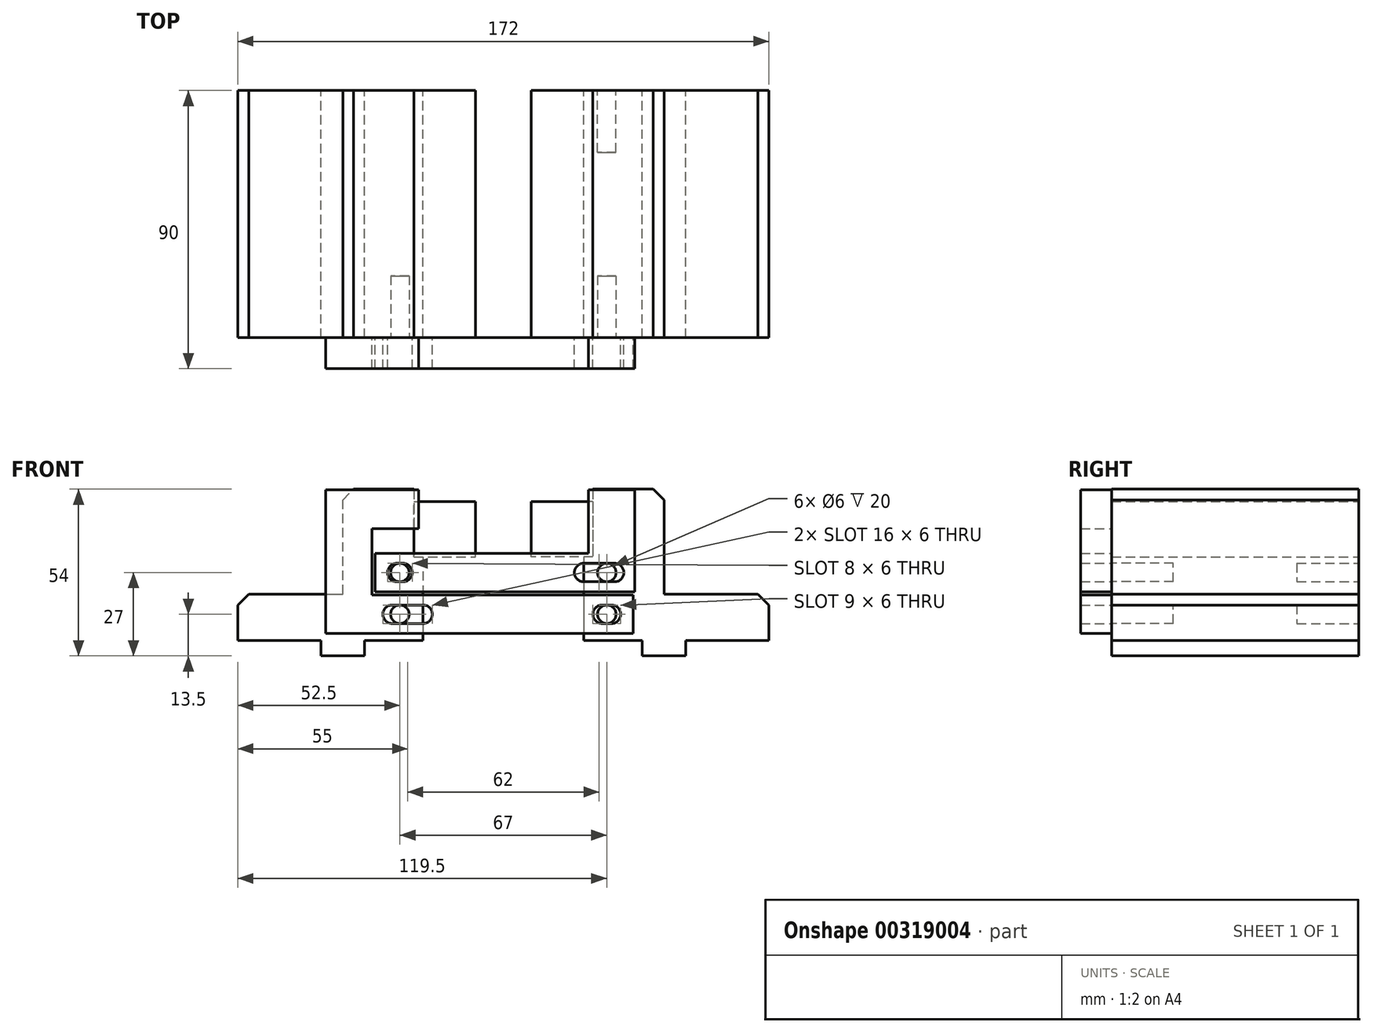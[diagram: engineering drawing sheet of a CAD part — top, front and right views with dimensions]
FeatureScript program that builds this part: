
annotation { "Feature Type Name" : "Feature", "Feature Type Description" : "" }
export const myFeature = defineFeature(function(context is Context, id is Id, definition is map)
    precondition{}
    {
        {
            var Q0;
            Q0=qCreatedBy(makeId("Front.planeOp"),FACE);
            var sketch = newSketch(context, id + "F0", { "sketchPlane" : qUnion([Q0])});
            skLineSegment(sketch, "E0", {"start": v(-26, 0) * mm, "end": v(-45, 0) * mm});
            skLineSegment(sketch, "E1", {"start": v(-45, 0) * mm, "end": v(-45, -5) * mm});
            skLineSegment(sketch, "E2", {"start": v(-45, -5) * mm, "end": v(-59, -5) * mm});
            skLineSegment(sketch, "E3", {"start": v(-59, -5) * mm, "end": v(-59, 0) * mm});
            skLineSegment(sketch, "E4", {"start": v(-59, 0) * mm, "end": v(-86, 0) * mm});
            skLineSegment(sketch, "E5", {"start": v(-86, 0) * mm, "end": v(-86, 11.46) * mm});
            skLineSegment(sketch, "E6", {"start": v(-86, 11.46) * mm, "end": v(-82.46, 15) * mm});
            skLineSegment(sketch, "E7", {"start": v(-82.46, 15) * mm, "end": v(-52, 15) * mm});
            skLineSegment(sketch, "E8", {"start": v(-52, 15) * mm, "end": v(-52, 45.46) * mm});
            skLineSegment(sketch, "E9", {"start": v(-52, 45.46) * mm, "end": v(-48.46, 49) * mm});
            skLineSegment(sketch, "E10", {"start": v(-48.46, 49) * mm, "end": v(-29, 49) * mm});
            skLineSegment(sketch, "E11", {"start": v(-29, 49) * mm, "end": v(-29, 45) * mm});
            skLineSegment(sketch, "E12", {"start": v(-29, 45) * mm, "end": v(-26, 45) * mm});
            skLineSegment(sketch, "E13", {"start": v(-26, 45) * mm, "end": v(-26, 0) * mm});
            skLineSegment(sketch, "E14.MirrorCS", {"start": v(45, 0) * mm, "end": v(45, -5) * mm});
            skLineSegment(sketch, "E15.MirrorCS", {"start": v(59, -5) * mm, "end": v(59, 0) * mm});
            skLineSegment(sketch, "E16.MirrorCS", {"start": v(29, 45) * mm, "end": v(26, 45) * mm});
            skLineSegment(sketch, "E17.MirrorCS", {"start": v(29, 49) * mm, "end": v(29, 45) * mm});
            skLineSegment(sketch, "E18.MirrorCS", {"start": v(86, 11.46) * mm, "end": v(82.46, 15) * mm});
            skLineSegment(sketch, "E19.MirrorCS", {"start": v(52, 45.46) * mm, "end": v(48.46, 49) * mm});
            skLineSegment(sketch, "E20.MirrorCS", {"start": v(26, 0) * mm, "end": v(45, 0) * mm});
            skLineSegment(sketch, "E21.MirrorCS", {"start": v(45, -5) * mm, "end": v(59, -5) * mm});
            skLineSegment(sketch, "E22.MirrorCS", {"start": v(26, 45) * mm, "end": v(26, 0) * mm});
            skLineSegment(sketch, "E23.MirrorCS", {"start": v(86, 0) * mm, "end": v(86, 11.46) * mm});
            skLineSegment(sketch, "E24.MirrorCS", {"start": v(48.46, 49) * mm, "end": v(29, 49) * mm});
            skLineSegment(sketch, "E25.MirrorCS", {"start": v(52, 15) * mm, "end": v(52, 45.46) * mm});
            skLineSegment(sketch, "E26.MirrorCS", {"start": v(82.46, 15) * mm, "end": v(52, 15) * mm});
            skLineSegment(sketch, "E27.MirrorCS", {"start": v(59, 0) * mm, "end": v(86, 0) * mm});
            skSolve(sketch);
        }
        {
            var Q0;
            Q0=makeQuery(id+"F0.imprint","IMPRINT",FACE,{"disambiguationData":[TD([[makeQuery(id+"F0.imprint","IMPRINT",EDGE,{"derivedFrom":sQuery(id+"F0.wireOp",EDGE,"E0")}),-1.0]])]});
            var Q1;
            Q1=makeQuery(id+"F0.imprint","IMPRINT",FACE,{"disambiguationData":[TD([[makeQuery(id+"F0.imprint","IMPRINT",EDGE,{"derivedFrom":sQuery(id+"F0.wireOp",EDGE,"E14.MirrorCS")}),1.0]])]});
            extrude(context, id + "F1", {"entities" : qUnion([Q0, Q1]), "endBound" : BoundingType.SYMMETRIC, "depth" : 80 * mm});
        }
        {
            var Q0;
            Q0=makeQuery(id+"F1.opExtrude","CAP_FACE",FACE,{"disambiguationData":[OSD([sQuery(id+"F0.wireOp",EDGE,"E14.MirrorCS"),sQuery(id+"F0.wireOp",EDGE,"E15.MirrorCS"),sQuery(id+"F0.wireOp",EDGE,"E16.MirrorCS"),sQuery(id+"F0.wireOp",EDGE,"E17.MirrorCS"),sQuery(id+"F0.wireOp",EDGE,"E18.MirrorCS"),sQuery(id+"F0.wireOp",EDGE,"E19.MirrorCS"),sQuery(id+"F0.wireOp",EDGE,"E20.MirrorCS"),sQuery(id+"F0.wireOp",EDGE,"E21.MirrorCS"),sQuery(id+"F0.wireOp",EDGE,"E22.MirrorCS"),sQuery(id+"F0.wireOp",EDGE,"E23.MirrorCS"),sQuery(id+"F0.wireOp",EDGE,"E24.MirrorCS"),sQuery(id+"F0.wireOp",EDGE,"E25.MirrorCS"),sQuery(id+"F0.wireOp",EDGE,"E26.MirrorCS"),sQuery(id+"F0.wireOp",EDGE,"E27.MirrorCS")])],"isStart":true});
            var sketch = newSketch(context, id + "F2", { "sketchPlane" : qUnion([Q0])});
            skLineSegment(sketch, "E28", {"start": v(-29, 45) * mm, "end": v(-29, 27) * mm});
            skLineSegment(sketch, "E29", {"start": v(-29, 27) * mm, "end": v(-26, 27) * mm});
            skSolve(sketch);
        }
        {
            var Q0;
            Q0=makeQuery(id+"F1.opExtrude","CAP_FACE",FACE,{"disambiguationData":[OSD([sQuery(id+"F0.wireOp",EDGE,"E0"),sQuery(id+"F0.wireOp",EDGE,"E1"),sQuery(id+"F0.wireOp",EDGE,"E2"),sQuery(id+"F0.wireOp",EDGE,"E3"),sQuery(id+"F0.wireOp",EDGE,"E4"),sQuery(id+"F0.wireOp",EDGE,"E5"),sQuery(id+"F0.wireOp",EDGE,"E6"),sQuery(id+"F0.wireOp",EDGE,"E7"),sQuery(id+"F0.wireOp",EDGE,"E8"),sQuery(id+"F0.wireOp",EDGE,"E9"),sQuery(id+"F0.wireOp",EDGE,"E10"),sQuery(id+"F0.wireOp",EDGE,"E11"),sQuery(id+"F0.wireOp",EDGE,"E12"),sQuery(id+"F0.wireOp",EDGE,"E13")])],"isStart":true});
            var sketch = newSketch(context, id + "F3", { "sketchPlane" : qUnion([Q0])});
            skLineSegment(sketch, "E30", {"start": v(29, 45) * mm, "end": v(29, 27) * mm});
            skLineSegment(sketch, "E31", {"start": v(29, 27) * mm, "end": v(26, 27) * mm});
            skSolve(sketch);
        }
        {
            var Q0;
            Q0=makeQuery(id+"F2.imprint","IMPRINT",FACE,{"disambiguationData":[TD([[makeQuery(id+"F2.imprint","IMPRINT",EDGE,{"derivedFrom":sQuery(id+"F2.wireOp",EDGE,"E28")}),1.0]])]});
            var Q1;
            Q1=makeQuery(id+"F3.imprint","IMPRINT",FACE,{"disambiguationData":[TD([[makeQuery(id+"F3.imprint","IMPRINT",EDGE,{"derivedFrom":sQuery(id+"F3.wireOp",EDGE,"E30")}),-1.0]])]});
            extrude(context, id + "F4", {"entities" : qUnion([Q0, Q1]), "operationType" : NewBodyOperationType.REMOVE, "oppositeDirection" : true, "depth" : 80 * mm});
        }
        {
            var Q0;
            Q0=makeQuery(id+"F1.opExtrude","CAP_FACE",FACE,{"disambiguationData":[OSD([sQuery(id+"F0.wireOp",EDGE,"E0"),sQuery(id+"F0.wireOp",EDGE,"E1"),sQuery(id+"F0.wireOp",EDGE,"E2"),sQuery(id+"F0.wireOp",EDGE,"E3"),sQuery(id+"F0.wireOp",EDGE,"E4"),sQuery(id+"F0.wireOp",EDGE,"E5"),sQuery(id+"F0.wireOp",EDGE,"E6"),sQuery(id+"F0.wireOp",EDGE,"E7"),sQuery(id+"F0.wireOp",EDGE,"E8"),sQuery(id+"F0.wireOp",EDGE,"E9"),sQuery(id+"F0.wireOp",EDGE,"E10"),sQuery(id+"F0.wireOp",EDGE,"E11"),sQuery(id+"F0.wireOp",EDGE,"E12"),sQuery(id+"F0.wireOp",EDGE,"E13")])],"isStart":false});
            var sketch = newSketch(context, id + "F5", { "sketchPlane" : qUnion([Q0])});
            skCircle(sketch, "E32", {"center": v(-33.5, 22) * mm, "radius": 3 * mm});
            skLineSegment(sketch, "E33.bottom", {"start": v(-41.5, 15.75) * mm, "end": v(42.5, 15.75) * mm});
            skLineSegment(sketch, "E33.top", {"start": v(-41.5, 28.25) * mm, "end": v(42.5, 28.25) * mm});
            skLineSegment(sketch, "E33.left", {"start": v(-41.5, 15.75) * mm, "end": v(-41.5, 28.25) * mm});
            skLineSegment(sketch, "E33.right", {"start": v(42.5, 15.75) * mm, "end": v(42.5, 28.25) * mm});
            skLineSegment(sketch, "E34.bottom", {"start": v(42.5, 28.25) * mm, "end": v(27.5, 28.25) * mm});
            skLineSegment(sketch, "E34.top", {"start": v(42.5, 48.75) * mm, "end": v(27.5, 48.75) * mm});
            skLineSegment(sketch, "E34.left", {"start": v(42.5, 28.25) * mm, "end": v(42.5, 48.75) * mm});
            skLineSegment(sketch, "E34.right", {"start": v(27.5, 28.25) * mm, "end": v(27.5, 48.75) * mm});
            skPoint(sketch, "E35.firstSnap0", {"position": v(27.5, 38.5) * mm});
            skLineSegment(sketch, "E36.bottom", {"start": v(-32.5, 25) * mm, "end": v(-34.5, 25) * mm});
            skLineSegment(sketch, "E36.top", {"start": v(-32.5, 19) * mm, "end": v(-34.5, 19) * mm});
            skLineSegment(sketch, "E36.left", {"start": v(-32.5, 25) * mm, "end": v(-32.5, 19) * mm});
            skLineSegment(sketch, "E36.right", {"start": v(-34.5, 25) * mm, "end": v(-34.5, 19) * mm});
            skArc(sketch, "E37", {"start": v(-32.5, 19) * mm, "mid": v(-29.5, 22) * mm, "end": v(-32.5, 25) * mm});
            skArc(sketch, "E38", {"start": v(-34.5, 25) * mm, "mid": v(-37.5, 22) * mm, "end": v(-34.5, 19) * mm});
            skCircle(sketch, "E39", {"center": v(33.5, 22) * mm, "radius": 3 * mm});
            skLineSegment(sketch, "E40.bottom", {"start": v(36, 25) * mm, "end": v(26, 25) * mm});
            skLineSegment(sketch, "E40.top", {"start": v(36, 19) * mm, "end": v(26, 19) * mm});
            skPoint(sketch, "E40.middle", {"position": v(31, 22) * mm});
            skArc(sketch, "E41", {"start": v(26, 25) * mm, "mid": v(23, 22) * mm, "end": v(26, 19) * mm});
            skArc(sketch, "E42", {"start": v(36, 19) * mm, "mid": v(39, 22) * mm, "end": v(36, 25) * mm});
            skSolve(sketch);
        }
        {
            var Q0;
            Q0 = qSketchRegion(id + "F5", true);
            extrude(context, id + "F6", {"entities" : qUnion([Q0]), "depth" : 10 * mm});
        }
        {
            var Q0;
            {var subQ0=sQuery(id+"F5.wireOp",EDGE,"E39");var subQ1=makeQuery(id+"F5.imprint","INTERSECT",VERTEX,{"derivedFrom":[subQ0,sQuery(id+"F5.wireOp",EDGE,"maQQuO1E-bkWu-ZeJO-gAS2-8m0wIhBBCGEc.bottom")]});Q0=makeQuery(id+"F5.imprint","IMPRINT",FACE,{"disambiguationData":[TD([[makeQuery(id+"F5.imprint","IMPRINT",EDGE,{"disambiguationData":[TD([[subQ1,1.0]])],"derivedFrom":subQ0}),1.0]])]});}
            var Q1;
            {var subQ0=sQuery(id+"F5.wireOp",EDGE,"E32");var subQ6=makeQuery(id+"F5.imprint","INTERSECT",VERTEX,{"derivedFrom":[subQ0,sQuery(id+"F5.wireOp",EDGE,"E36.bottom")]});Q1=makeQuery(id+"F5.imprint","IMPRINT",FACE,{"disambiguationData":[TD([[makeQuery(id+"F5.imprint","IMPRINT",EDGE,{"disambiguationData":[TD([[subQ6,1.0]])],"derivedFrom":subQ0}),1.0]])]});}
            var Q2;
            {var subQ0=sQuery(id+"F5.wireOp",EDGE,"E36.right");var subQ1=sQuery(id+"F5.wireOp",EDGE,"E32");var subQ2=makeQuery(id+"F5.imprint","INTERSECT",VERTEX,{"disambiguationData":[OD(0.0)],"derivedFrom":[subQ1,subQ0]});Q2=makeQuery(id+"F5.imprint","IMPRINT",FACE,{"disambiguationData":[TD([[makeQuery(id+"F5.imprint","IMPRINT",EDGE,{"disambiguationData":[TD([[subQ2,-1.0]])],"derivedFrom":subQ1}),1.0]])]});}
            var Q3;
            {var subQ0=sQuery(id+"F5.wireOp",EDGE,"E36.left");var subQ1=sQuery(id+"F5.wireOp",EDGE,"E32");var subQ2=makeQuery(id+"F5.imprint","INTERSECT",VERTEX,{"disambiguationData":[OD(0.0)],"derivedFrom":[subQ1,subQ0]});Q3=makeQuery(id+"F5.imprint","IMPRINT",FACE,{"disambiguationData":[TD([[makeQuery(id+"F5.imprint","IMPRINT",EDGE,{"disambiguationData":[TD([[subQ2,1.0]])],"derivedFrom":subQ1}),1.0]])]});}
            extrude(context, id + "F7", {"entities" : qUnion([Q0, Q1, Q2, Q3]), "operationType" : NewBodyOperationType.REMOVE, "oppositeDirection" : true, "depth" : 20 * mm});
        }
        {
            var Q0;
            Q0=makeQuery(id+"F1.opExtrude","CAP_FACE",FACE,{"disambiguationData":[OSD([sQuery(id+"F0.wireOp",EDGE,"E0"),sQuery(id+"F0.wireOp",EDGE,"E1"),sQuery(id+"F0.wireOp",EDGE,"E2"),sQuery(id+"F0.wireOp",EDGE,"E3"),sQuery(id+"F0.wireOp",EDGE,"E4"),sQuery(id+"F0.wireOp",EDGE,"E5"),sQuery(id+"F0.wireOp",EDGE,"E6"),sQuery(id+"F0.wireOp",EDGE,"E7"),sQuery(id+"F0.wireOp",EDGE,"E8"),sQuery(id+"F0.wireOp",EDGE,"E9"),sQuery(id+"F0.wireOp",EDGE,"E10"),sQuery(id+"F0.wireOp",EDGE,"E11"),sQuery(id+"F0.wireOp",EDGE,"E12"),sQuery(id+"F0.wireOp",EDGE,"E13")])],"isStart":false});
            var sketch = newSketch(context, id + "F8", { "sketchPlane" : qUnion([Q0])});
            skSolve(sketch);
        }
        {
            var Q0;
            Q0=makeQuery(id+"F8.imprint","IMPRINT",FACE,{"disambiguationData":[TD([[makeQuery(id+"F8.imprint","IMPRINT",EDGE,{"derivedFrom":makeQuery(id+"F1.opExtrude","CAP_EDGE",EDGE,{"disambiguationData":[OSD([sQuery(id+"F0.wireOp",EDGE,"E0")])],"isStart":false})}),-1.0]])]});
            var sketch = newSketch(context, id + "F9", { "sketchPlane" : qUnion([Q0])});
            skCircle(sketch, "E43", {"center": v(-33.5, 8.5) * mm, "radius": 3 * mm});
            skCircle(sketch, "E44", {"center": v(33.5, 8.5) * mm, "radius": 3 * mm});
            skLineSegment(sketch, "E45.bottom", {"start": v(-57.5, 2.25) * mm, "end": v(42, 2.25) * mm});
            skLineSegment(sketch, "E45.top", {"start": v(-57.5, 14.75) * mm, "end": v(42, 14.75) * mm});
            skLineSegment(sketch, "E45.left", {"start": v(-57.5, 2.25) * mm, "end": v(-57.5, 14.75) * mm});
            skLineSegment(sketch, "E45.right", {"start": v(42, 2.25) * mm, "end": v(42, 14.75) * mm});
            skLineSegment(sketch, "E46.bottom", {"start": v(-57.5, 14.75) * mm, "end": v(-42.5, 14.75) * mm});
            skLineSegment(sketch, "E46.top", {"start": v(-57.5, 48.75) * mm, "end": v(-42.5, 48.75) * mm});
            skLineSegment(sketch, "E46.left", {"start": v(-57.5, 14.75) * mm, "end": v(-57.5, 48.75) * mm});
            skLineSegment(sketch, "E46.right", {"start": v(-42.5, 14.75) * mm, "end": v(-42.5, 48.75) * mm});
            skLineSegment(sketch, "E47.bottom", {"start": v(-42.5, 36.25) * mm, "end": v(-27.5, 36.25) * mm});
            skLineSegment(sketch, "E47.top", {"start": v(-42.5, 48.75) * mm, "end": v(-27.5, 48.75) * mm});
            skLineSegment(sketch, "E47.left", {"start": v(-42.5, 36.25) * mm, "end": v(-42.5, 48.75) * mm});
            skLineSegment(sketch, "E47.right", {"start": v(-27.5, 36.25) * mm, "end": v(-27.5, 48.75) * mm});
            skLineSegment(sketch, "E48.bottom", {"start": v(-26, 11.5) * mm, "end": v(-36, 11.5) * mm});
            skLineSegment(sketch, "E48.top", {"start": v(-26, 5.5) * mm, "end": v(-36, 5.5) * mm});
            skPoint(sketch, "E48.middle", {"position": v(-31, 8.5) * mm});
            skArc(sketch, "E49", {"start": v(-26, 5.5) * mm, "mid": v(-23, 8.5) * mm, "end": v(-26, 11.5) * mm});
            skArc(sketch, "E50", {"start": v(-36, 11.5) * mm, "mid": v(-39, 8.5) * mm, "end": v(-36, 5.5) * mm});
            skLineSegment(sketch, "E51.bottom", {"start": v(35, 11.5) * mm, "end": v(32, 11.5) * mm});
            skLineSegment(sketch, "E51.top", {"start": v(35, 5.5) * mm, "end": v(32, 5.5) * mm});
            skLineSegment(sketch, "E51.left", {"start": v(35, 11.5) * mm, "end": v(35, 5.5) * mm});
            skLineSegment(sketch, "E51.right", {"start": v(32, 11.5) * mm, "end": v(32, 5.5) * mm});
            skArc(sketch, "E52", {"start": v(32, 11.5) * mm, "mid": v(29, 8.5) * mm, "end": v(32, 5.5) * mm});
            skArc(sketch, "E53", {"start": v(35, 5.5) * mm, "mid": v(38, 8.5) * mm, "end": v(35, 11.5) * mm});
            skSolve(sketch);
        }
        {
            var Q0;
            {var subQ0=sQuery(id+"F9.wireOp",EDGE,"E43");var subQ1=makeQuery(id+"F9.imprint","INTERSECT",VERTEX,{"derivedFrom":[subQ0,sQuery(id+"F9.wireOp",EDGE,"E48.bottom")]});Q0=makeQuery(id+"F9.imprint","IMPRINT",FACE,{"disambiguationData":[TD([[makeQuery(id+"F9.imprint","IMPRINT",EDGE,{"disambiguationData":[TD([[subQ1,-1.0]])],"derivedFrom":subQ0}),1.0]])]});}
            var Q1;
            {var subQ0=sQuery(id+"F9.wireOp",EDGE,"E51.right");var subQ1=sQuery(id+"F9.wireOp",EDGE,"E44");var subQ2=makeQuery(id+"F9.imprint","INTERSECT",VERTEX,{"disambiguationData":[OD(0.0)],"derivedFrom":[subQ1,subQ0]});Q1=makeQuery(id+"F9.imprint","IMPRINT",FACE,{"disambiguationData":[TD([[makeQuery(id+"F9.imprint","IMPRINT",EDGE,{"disambiguationData":[TD([[subQ2,-1.0]])],"derivedFrom":subQ1}),1.0]])]});}
            var Q2;
            {var subQ0=sQuery(id+"F9.wireOp",EDGE,"E44");var subQ6=makeQuery(id+"F9.imprint","INTERSECT",VERTEX,{"derivedFrom":[subQ0,sQuery(id+"F9.wireOp",EDGE,"E51.bottom")]});Q2=makeQuery(id+"F9.imprint","IMPRINT",FACE,{"disambiguationData":[TD([[makeQuery(id+"F9.imprint","IMPRINT",EDGE,{"disambiguationData":[TD([[subQ6,1.0]])],"derivedFrom":subQ0}),1.0]])]});}
            var Q3;
            {var subQ0=sQuery(id+"F9.wireOp",EDGE,"E51.left");var subQ1=sQuery(id+"F9.wireOp",EDGE,"E44");var subQ2=makeQuery(id+"F9.imprint","INTERSECT",VERTEX,{"disambiguationData":[OD(0.0)],"derivedFrom":[subQ1,subQ0]});Q3=makeQuery(id+"F9.imprint","IMPRINT",FACE,{"disambiguationData":[TD([[makeQuery(id+"F9.imprint","IMPRINT",EDGE,{"disambiguationData":[TD([[subQ2,1.0]])],"derivedFrom":subQ1}),1.0]])]});}
            var Q4;
            Q4=sQuery(id+"F9.wireOp",EDGE,"E43");
            var Q5;
            Q5=sQuery(id+"F9.wireOp",EDGE,"E44");
            extrude(context, id + "F10", {"entities" : qUnion([Q0, Q1, Q2, Q3]), "operationType" : NewBodyOperationType.REMOVE, "surfaceEntities" : qUnion([Q4, Q5]), "oppositeDirection" : true, "depth" : 20 * mm});
        }
        {
            var Q0;
            Q0 = qSketchRegion(id + "F9", true);
            extrude(context, id + "F11", {"entities" : qUnion([Q0]), "depth" : 10 * mm});
        }
        {
            var Q0;
            Q0=makeQuery(id+"F1.opExtrude","CAP_FACE",FACE,{"disambiguationData":[OSD([sQuery(id+"F0.wireOp",EDGE,"E14.MirrorCS"),sQuery(id+"F0.wireOp",EDGE,"E15.MirrorCS"),sQuery(id+"F0.wireOp",EDGE,"E16.MirrorCS"),sQuery(id+"F0.wireOp",EDGE,"E17.MirrorCS"),sQuery(id+"F0.wireOp",EDGE,"E18.MirrorCS"),sQuery(id+"F0.wireOp",EDGE,"E19.MirrorCS"),sQuery(id+"F0.wireOp",EDGE,"E20.MirrorCS"),sQuery(id+"F0.wireOp",EDGE,"E21.MirrorCS"),sQuery(id+"F0.wireOp",EDGE,"E22.MirrorCS"),sQuery(id+"F0.wireOp",EDGE,"E23.MirrorCS"),sQuery(id+"F0.wireOp",EDGE,"E24.MirrorCS"),sQuery(id+"F0.wireOp",EDGE,"E25.MirrorCS"),sQuery(id+"F0.wireOp",EDGE,"E26.MirrorCS"),sQuery(id+"F0.wireOp",EDGE,"E27.MirrorCS")])],"isStart":true});
            var sketch = newSketch(context, id + "F12", { "sketchPlane" : qUnion([Q0])});
            skLineSegment(sketch, "E54.bottom", {"start": v(-29, 27) * mm, "end": v(-9, 27) * mm});
            skLineSegment(sketch, "E54.top", {"start": v(-29, 45) * mm, "end": v(-9, 45) * mm});
            skLineSegment(sketch, "E54.left", {"start": v(-29, 27) * mm, "end": v(-29, 45) * mm});
            skLineSegment(sketch, "E54.right", {"start": v(-9, 27) * mm, "end": v(-9, 45) * mm});
            skLineSegment(sketch, "E55.MirrorCS", {"start": v(9, 27) * mm, "end": v(9, 45) * mm});
            skLineSegment(sketch, "E56.MirrorCS", {"start": v(29, 45) * mm, "end": v(9, 45) * mm});
            skLineSegment(sketch, "E57.MirrorCS", {"start": v(29, 27) * mm, "end": v(9, 27) * mm});
            skLineSegment(sketch, "E58.MirrorCS", {"start": v(29, 27) * mm, "end": v(29, 45) * mm});
            skSolve(sketch);
        }
        {
            var Q0;
            Q0 = qSketchRegion(id + "F12", true);
            extrude(context, id + "F13", {"entities" : qUnion([Q0]), "oppositeDirection" : true, "depth" : 80 * mm});
        }
        {
            var Q0;
            Q0=makeQuery(id+"F1.opExtrude","CAP_FACE",FACE,{"disambiguationData":[OSD([sQuery(id+"F0.wireOp",EDGE,"E14.MirrorCS"),sQuery(id+"F0.wireOp",EDGE,"E15.MirrorCS"),sQuery(id+"F0.wireOp",EDGE,"E16.MirrorCS"),sQuery(id+"F0.wireOp",EDGE,"E17.MirrorCS"),sQuery(id+"F0.wireOp",EDGE,"E18.MirrorCS"),sQuery(id+"F0.wireOp",EDGE,"E19.MirrorCS"),sQuery(id+"F0.wireOp",EDGE,"E20.MirrorCS"),sQuery(id+"F0.wireOp",EDGE,"E21.MirrorCS"),sQuery(id+"F0.wireOp",EDGE,"E22.MirrorCS"),sQuery(id+"F0.wireOp",EDGE,"E23.MirrorCS"),sQuery(id+"F0.wireOp",EDGE,"E24.MirrorCS"),sQuery(id+"F0.wireOp",EDGE,"E25.MirrorCS"),sQuery(id+"F0.wireOp",EDGE,"E26.MirrorCS"),sQuery(id+"F0.wireOp",EDGE,"E27.MirrorCS")])],"isStart":true});
            var sketch = newSketch(context, id + "F14", { "sketchPlane" : qUnion([Q0])});
            skCircle(sketch, "E59", {"center": v(-33.5, 22) * mm, "radius": 3 * mm});
            skCircle(sketch, "E60", {"center": v(-33.5, 8.5) * mm, "radius": 3 * mm});
            skCircle(sketch, "E61.MirrorC", {"center": v(33.5, 22) * mm, "radius": 3 * mm});
            skCircle(sketch, "E62.MirrorC", {"center": v(33.5, 8.5) * mm, "radius": 3 * mm});
            skSolve(sketch);
        }
        {
            var Q0;
            Q0=makeQuery(id+"F14.imprint","IMPRINT",FACE,{"disambiguationData":[TD([[makeQuery(id+"F14.imprint","IMPRINT",EDGE,{"derivedFrom":sQuery(id+"F14.wireOp",EDGE,"E59")}),1.0]])]});
            var Q1;
            Q1=makeQuery(id+"F14.imprint","IMPRINT",FACE,{"disambiguationData":[TD([[makeQuery(id+"F14.imprint","IMPRINT",EDGE,{"derivedFrom":sQuery(id+"F14.wireOp",EDGE,"E60")}),1.0]])]});
            var Q2;
            Q2=makeQuery(id+"F14.imprint","IMPRINT",FACE,{"disambiguationData":[TD([[makeQuery(id+"F14.imprint","IMPRINT",EDGE,{"derivedFrom":sQuery(id+"F14.wireOp",EDGE,"E62.MirrorC")}),-1.0]])]});
            var Q3;
            Q3=makeQuery(id+"F14.imprint","IMPRINT",FACE,{"disambiguationData":[TD([[makeQuery(id+"F14.imprint","IMPRINT",EDGE,{"derivedFrom":sQuery(id+"F14.wireOp",EDGE,"E61.MirrorC")}),-1.0]])]});
            extrude(context, id + "F15", {"entities" : qUnion([Q0, Q1, Q2, Q3]), "operationType" : NewBodyOperationType.REMOVE, "oppositeDirection" : true, "depth" : 20 * mm});
        }
    });
